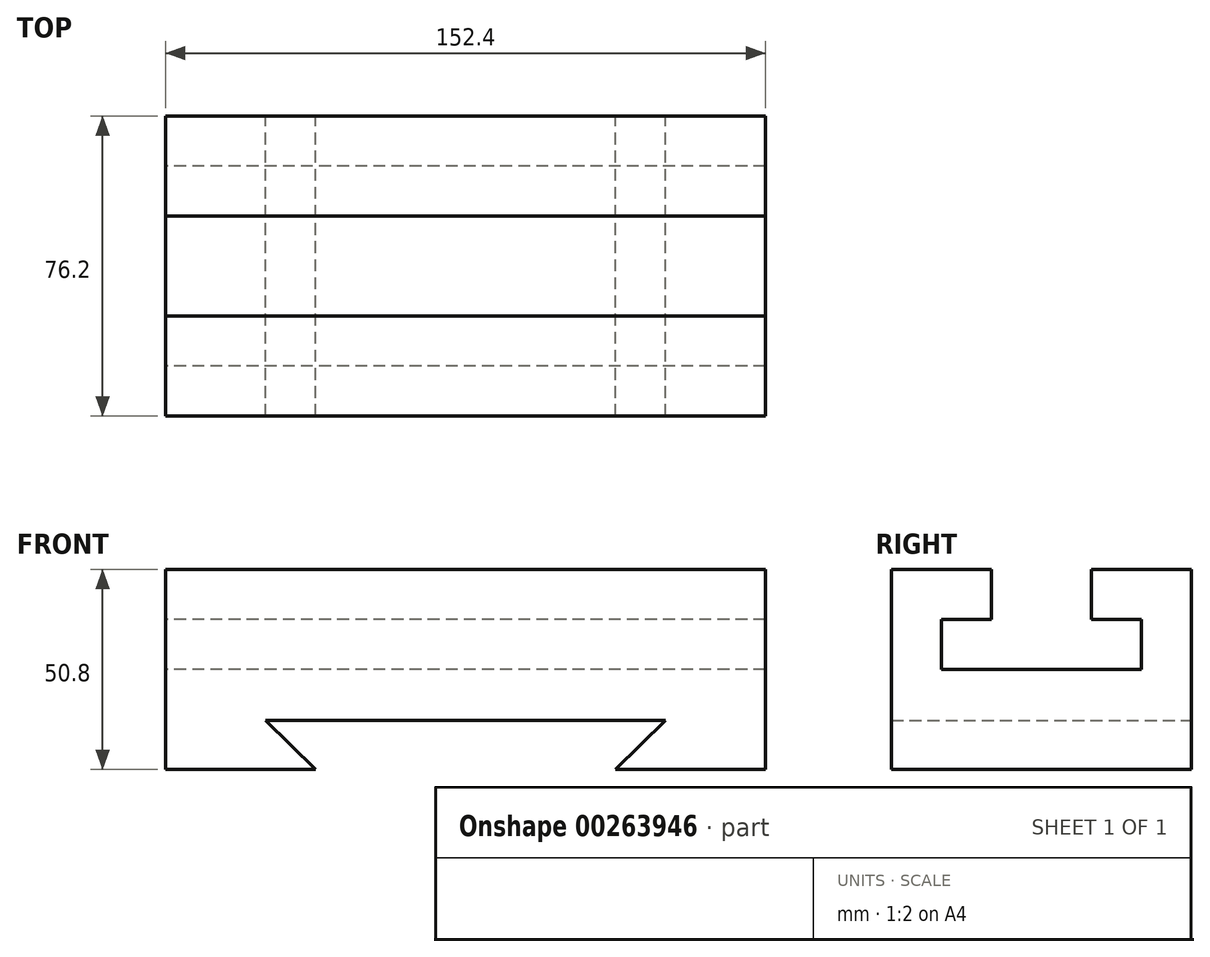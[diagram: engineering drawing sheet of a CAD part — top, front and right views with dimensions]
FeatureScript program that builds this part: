
annotation { "Feature Type Name" : "Feature", "Feature Type Description" : "" }
export const myFeature = defineFeature(function(context is Context, id is Id, definition is map)
    precondition{}
    {
        {
            var Q0;
            Q0=qCreatedBy(makeId("Right.planeOp"),FACE);
            var sketch = newSketch(context, id + "F0", { "sketchPlane" : qUnion([Q0])});
            skLineSegment(sketch, "E0", {"start": v(-41.44, 0) * mm, "end": v(34.76, 0) * mm});
            skLineSegment(sketch, "E1", {"start": v(34.76, 0) * mm, "end": v(34.76, 50.8) * mm});
            skLineSegment(sketch, "E2", {"start": v(-41.44, 0) * mm, "end": v(-41.44, 50.8) * mm});
            skLineSegment(sketch, "E3", {"start": v(-41.44, 50.8) * mm, "end": v(-16.04, 50.8) * mm});
            skLineSegment(sketch, "E4", {"start": v(-16.04, 50.8) * mm, "end": v(-16.04, 38.1) * mm});
            skLineSegment(sketch, "E5", {"start": v(-16.04, 38.1) * mm, "end": v(-28.74, 38.1) * mm});
            skLineSegment(sketch, "E6", {"start": v(-28.74, 38.1) * mm, "end": v(-28.74, 25.4) * mm});
            skLineSegment(sketch, "E7", {"start": v(-28.74, 25.4) * mm, "end": v(22.06, 25.4) * mm});
            skLineSegment(sketch, "E8", {"start": v(22.06, 25.4) * mm, "end": v(22.06, 38.1) * mm});
            skLineSegment(sketch, "E9", {"start": v(22.06, 38.1) * mm, "end": v(9.36, 38.1) * mm});
            skLineSegment(sketch, "E10", {"start": v(9.36, 38.1) * mm, "end": v(9.36, 50.8) * mm});
            skLineSegment(sketch, "E11", {"start": v(9.36, 50.8) * mm, "end": v(34.76, 50.8) * mm});
            skSolve(sketch);
        }
        {
            var Q0;
            Q0 = qSketchRegion(id + "F0", true);
            extrude(context, id + "F1", {"entities" : qUnion([Q0]), "depth" : 152.4 * mm});
        }
        {
            var Q0;
            Q0=makeQuery(id+"F1.opExtrude","SWEPT_FACE",FACE,{"disambiguationData":[OSD([sQuery(id+"F0.wireOp",EDGE,"E1")])]});
            var sketch = newSketch(context, id + "F2", { "sketchPlane" : qUnion([Q0])});
            skSolve(sketch);
        }
        {
            var Q0;
            {var subQ0=sQuery(id+"F0.wireOp",EDGE,"E1");Q0=makeQuery(id+"F2.imprint","IMPRINT",FACE,{"disambiguationData":[TD([[makeQuery(id+"F2.imprint","IMPRINT",EDGE,{"derivedFrom":makeQuery(id+"F1.opExtrude","CAP_EDGE",EDGE,{"disambiguationData":[OSD([subQ0])],"isStart":true})}),1.0]])]});}
            var sketch = newSketch(context, id + "F3", { "sketchPlane" : qUnion([Q0])});
            skLineSegment(sketch, "E12", {"start": v(-114.3, 0) * mm, "end": v(-127, 12.44) * mm});
            skLineSegment(sketch, "E13", {"start": v(-127, 12.44) * mm, "end": v(-25.4, 12.44) * mm});
            skLineSegment(sketch, "E14", {"start": v(-25.4, 12.44) * mm, "end": v(-38.1, 0) * mm});
            skLineSegment(sketch, "E15", {"start": v(-38.1, 0) * mm, "end": v(-114.3, 0) * mm});
            skLineSegment(sketch, "E16", {"start": v(-152.4, 0) * mm, "end": v(-114.3, 0) * mm});
            skLineSegment(sketch, "E17", {"start": v(0, 0) * mm, "end": v(-38.1, 0) * mm});
            skSolve(sketch);
        }
        {
            var Q0;
            Q0 = qSketchRegion(id + "F3", true);
            extrude(context, id + "F4", {"entities" : qUnion([Q0]), "operationType" : NewBodyOperationType.REMOVE, "endBound" : BoundingType.UP_TO_NEXT, "oppositeDirection" : true, "depth" : 25.4 * mm});
        }
    });
